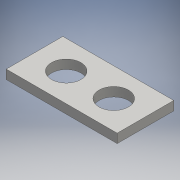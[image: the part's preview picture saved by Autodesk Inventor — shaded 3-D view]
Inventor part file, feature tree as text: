
AUTODESK INVENTOR PART (.ipt)
format: ipt  version: 2016 SP1 (Build 200210100, 210)  size: 99,328 bytes
history: native  units: mm
features: extrude x1, sketch x1
ambient origin geometry x8: Origin, YZ Plane, XZ Plane, XY Plane, X Axis, Y Axis, Z Axis, Center Point
bodies: Solid1 (feature_tree)
feature tree (2):
  extrude  "Extrusion1"  Depth=8.0mm
  sketch  "Sketch1"  dims[d0=26.0mm d1=26.0mm d2=42.0mm d3=21.0mm d4=25.0mm d5=50.0mm d6=15.0mm d7=15.0mm d8=8.0mm d9=0.0mm]
